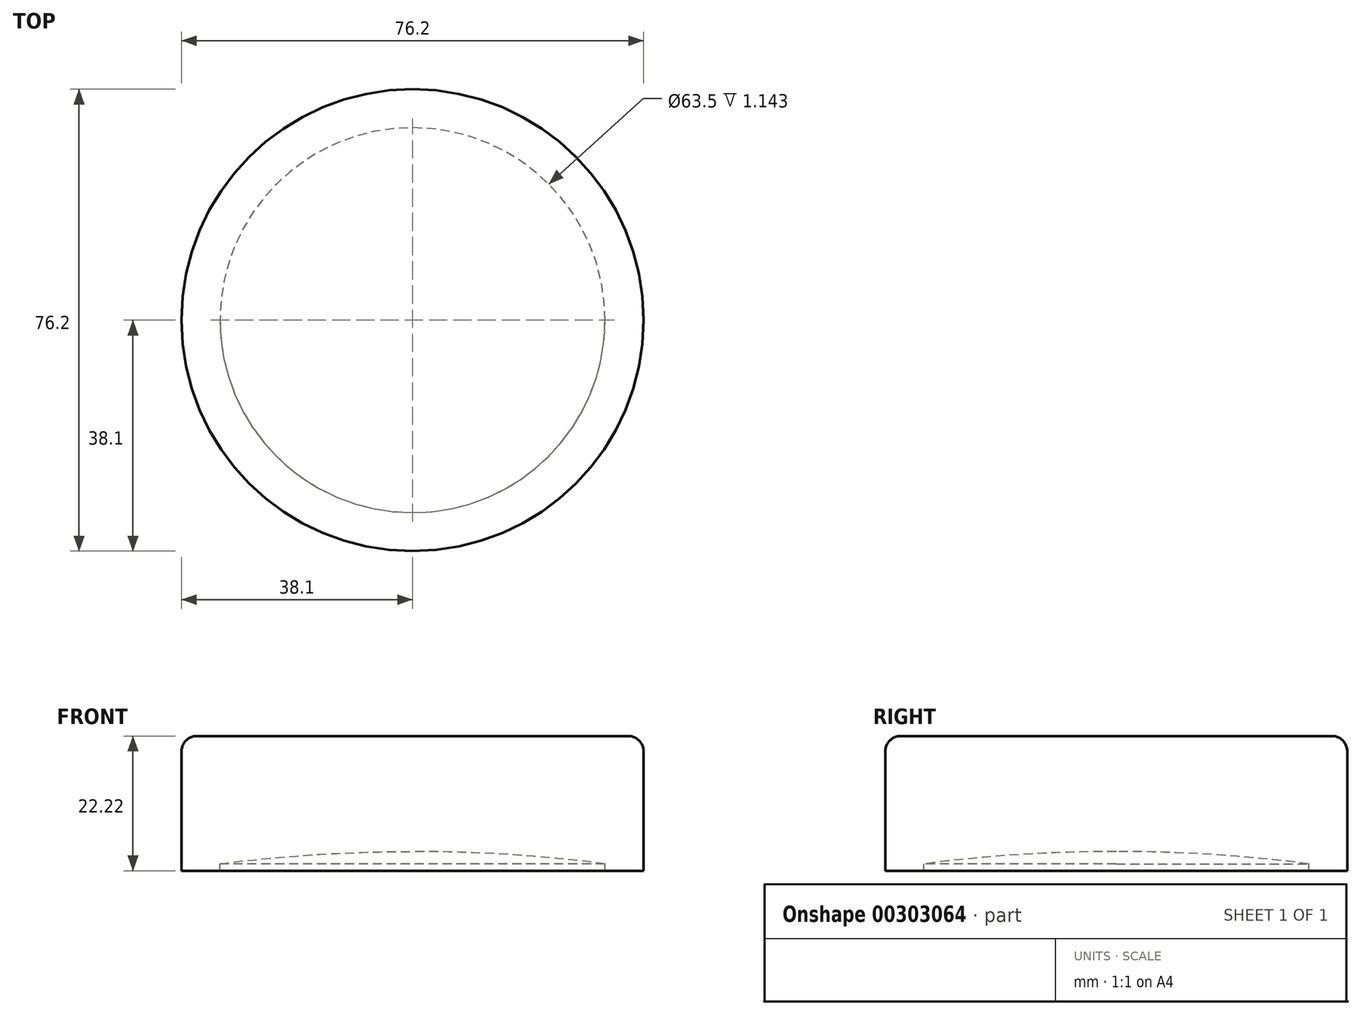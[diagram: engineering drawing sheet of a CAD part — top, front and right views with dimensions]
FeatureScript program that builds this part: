
annotation { "Feature Type Name" : "Feature", "Feature Type Description" : "" }
export const myFeature = defineFeature(function(context is Context, id is Id, definition is map)
    precondition{}
    {
        {
            var Q0;
            Q0=qCreatedBy(makeId("Front.planeOp"),FACE);
            var sketch = newSketch(context, id + "F0", { "sketchPlane" : qUnion([Q0])});
            skLineSegment(sketch, "E0.bottom", {"start": v(38.1, -11.11) * mm, "end": v(-38.1, -11.11) * mm});
            skLineSegment(sketch, "E0.top", {"start": v(35.56, 11.11) * mm, "end": v(-35.56, 11.11) * mm});
            skLineSegment(sketch, "E0.left", {"start": v(38.1, -11.11) * mm, "end": v(38.1, 8.57) * mm});
            skLineSegment(sketch, "E0.right", {"start": v(-38.1, -11.11) * mm, "end": v(-38.1, 8.57) * mm});
            skPoint(sketch, "E0.middle", {"position": v(0, 0) * mm});
            skPoint(sketch, "E1.visualSharp", {"position": v(-38.1, 11.11) * mm});
            skArc(sketch, "E1.filletArc", {"start": v(-35.56, 11.11) * mm, "mid": v(-37.36, 10.37) * mm, "end": v(-38.1, 8.57) * mm});
            skLineSegment(sketch, "E2", {"start": v(-31.75, -9.97) * mm, "end": v(-31.75, -11.11) * mm});
            skLineSegment(sketch, "E3", {"start": v(-31.75, -9.97) * mm, "end": v(31.75, -9.97) * mm});
            skLineSegment(sketch, "E4", {"start": v(31.75, -9.97) * mm, "end": v(31.75, -11.11) * mm});
            skArc(sketch, "E5", {"start": v(31.75, -9.97) * mm, "mid": v(0, -7.94) * mm, "end": v(-31.75, -9.97) * mm});
            skLineSegment(sketch, "E6", {"start": v(0, 33.92) * mm, "end": v(0, -44.4) * mm, "construction": true});
            skArc(sketch, "E7.MirrorCS", {"start": v(35.56, 11.11) * mm, "mid": v(37.36, 10.37) * mm, "end": v(38.1, 8.57) * mm});
            skPoint(sketch, "E8.orphan", {"position": v(38.1, 11.11) * mm});
            skLineSegment(sketch, "E9", {"start": v(0, 11.11) * mm, "end": v(0, -7.94) * mm});
            skSolve(sketch);
        }
        {
            var Q0;
            {var subQ1=sQuery(id+"F0.wireOp",EDGE,"E0.right");Q0=makeQuery(id+"F0.imprint","IMPRINT",FACE,{"disambiguationData":[TD([[makeQuery(id+"F0.imprint","IMPRINT",EDGE,{"derivedFrom":subQ1}),-1.0]])]});}
            var Q1;
            Q1=sQuery(id+"F0.wireOp",EDGE,"E6");
            revolve(context, id + "F1", {"entities" : qUnion([Q0]), "axis" : qUnion([Q1]), "revolveType" : RevolveType.FULL});
        }
    });
